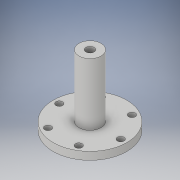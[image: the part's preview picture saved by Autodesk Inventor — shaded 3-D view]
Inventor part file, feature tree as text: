
AUTODESK INVENTOR PART (.ipt)
format: ipt  version: 2017 (Build 210142000, 142)  size: 145,408 bytes
history: native  units: in
note: dims shown in document units (in); Inventor stores cm internally (conversion verified against a paired STEP export)
features: sketch x3, revolve x1, extrude x1, hole x1, pattern_circular x1
ambient origin geometry x8: Origin, YZ Plane, XZ Plane, XY Plane, X Axis, Y Axis, Z Axis, Center Point
bodies: Solid1 (feature_tree)
feature tree (7):
  revolve  "Revolution1"  Angle=90.0deg
  extrude  "Extrusion1"  Depth=0.2047in
  hole  "Hole2"  [1 undecoded]
  pattern_circular  "Circular Pattern2"  [2 undecoded]
  sketch  "Sketch1"  dims[d0=1.0394in d14=90.0deg]
  sketch  "Sketch4"  dims[d23=0.935in d24=0.2047in]
  sketch  "Sketch5"  dims[d25=2.3622in d27=360.0deg d29=0.2362in d30=0.0in d39=0.385in d40=45.0deg d42=0.104in d43=0.2in d44=0.375in d45=0.25in d46=0.5635in d47=0.2in d48=0.8108in d53=1.8895in d54=1.5748in d55=360.0deg]
note: 3 required parameter values undecoded (feature->parameter linkage not recoverable at this tier; creation-order binding heuristic only, values carry confidence <= 0.55)
